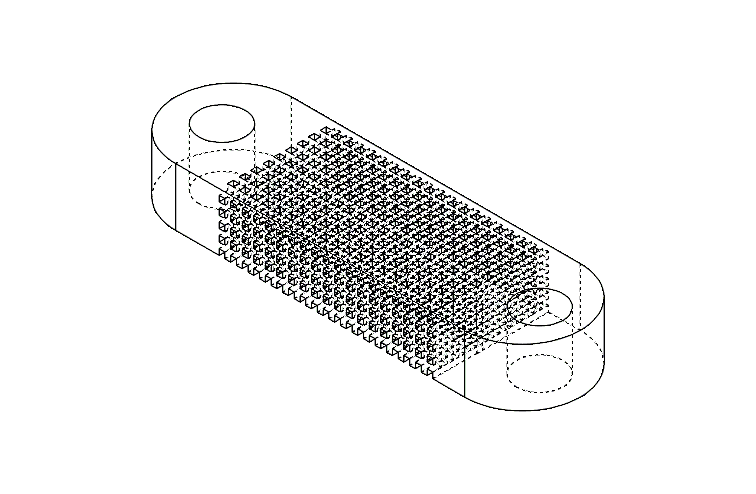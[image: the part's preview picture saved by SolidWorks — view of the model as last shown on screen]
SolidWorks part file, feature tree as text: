
SOLIDWORKS PART (.sldprt)
format: sldprt  version: not decoded by parser v0  size: 2,415,616 bytes
history: native  units: mm
features: sketch x15, cut_extrude x12, pattern_linear x10, extrude x3, material x1 (+13 scaffold rows collapsed)
feature tree (54):
  scaffold x13  (default folders/planes/origin — collapsed)
  material  "Material <not specified>"
  sketch  "Sketch2"
  extrude  "Boss-Extrude1"  Depth=10mm
  sketch  "Sketch3"  dims[D1=~8.687516mm]
  extrude  "Boss-Extrude2"  Depth=10mm
  sketch  "Sketch4"  dims[D1=~10.018925mm]
  extrude  "Boss-Extrude3"  Depth=10mm
  sketch  "Sketch5"  dims[D1=~4.351407mm]
  cut_extrude  "Cut-Extrude1"  [1 undecoded]
  sketch  "Sketch6"  dims[D1=~3.44409mm]
  cut_extrude  "Cut-Extrude2"  [1 undecoded]
  sketch  "Sketch10"  dims[D1=1.0mm D2=1.0mm]
  cut_extrude  "Cut-Extrude6"  [1 undecoded]
  pattern_linear  "LPattern4"  Count1=19 Count2=1 Spacing1=2mm Spacing2=2mm
  sketch  "Sketch11"
  cut_extrude  "Cut-Extrude7"  [1 undecoded]
  pattern_linear  "LPattern5"  Count1=19 Count2=1 Spacing1=2mm Spacing2=2mm
  sketch  "Sketch12"
  cut_extrude  "Cut-Extrude8"  [1 undecoded]
  pattern_linear  "LPattern6"  Count1=19 Count2=1 Spacing1=2mm Spacing2=2mm
  sketch  "Sketch13"
  cut_extrude  "Cut-Extrude9"  [1 undecoded]
  pattern_linear  "LPattern7"  Count1=19 Count2=1 Spacing1=2mm Spacing2=2mm
  sketch  "Sketch14"
  cut_extrude  "Cut-Extrude10"  [1 undecoded]
  pattern_linear  "LPattern8"  Count1=19 Count2=1 Spacing1=2mm Spacing2=2mm
  sketch  "Sketch19"
  cut_extrude  "Cut-Extrude12"  [1 undecoded]
  pattern_linear  "LPattern10"  Count1=19 Count2=1 Spacing1=2mm Spacing2=2mm
  sketch  "Sketch20"
  cut_extrude  "Cut-Extrude13"  [1 undecoded]
  pattern_linear  "LPattern11"  Count1=19 Count2=1 Spacing1=2mm Spacing2=2mm
  sketch  "Sketch21"
  cut_extrude  "Cut-Extrude14"  Depth=10mm
  pattern_linear  "LPattern12"  Count1=19 Count2=1 Spacing1=2mm Spacing2=2mm
  sketch  "Sketch22"
  cut_extrude  "Cut-Extrude15"  [1 undecoded]
  pattern_linear  "LPattern13"  Count1=19 Count2=1 Spacing1=2mm Spacing2=2mm
  sketch  "Sketch27"
  cut_extrude  "Cut-Extrude16"  [1 undecoded]
  pattern_linear  "LPattern14"  Count1=19 Count2=5 Spacing1=2mm Spacing2=2mm
decode coverage: 19 of 40 modeling features carry decoded parameters
note: ~ marks probable driven/reference dimensions
note: 11 parameter values undecoded
summary: no parameter record found for 11 features
note: suppression state not decoded; provenance and decode notes live in map.json
